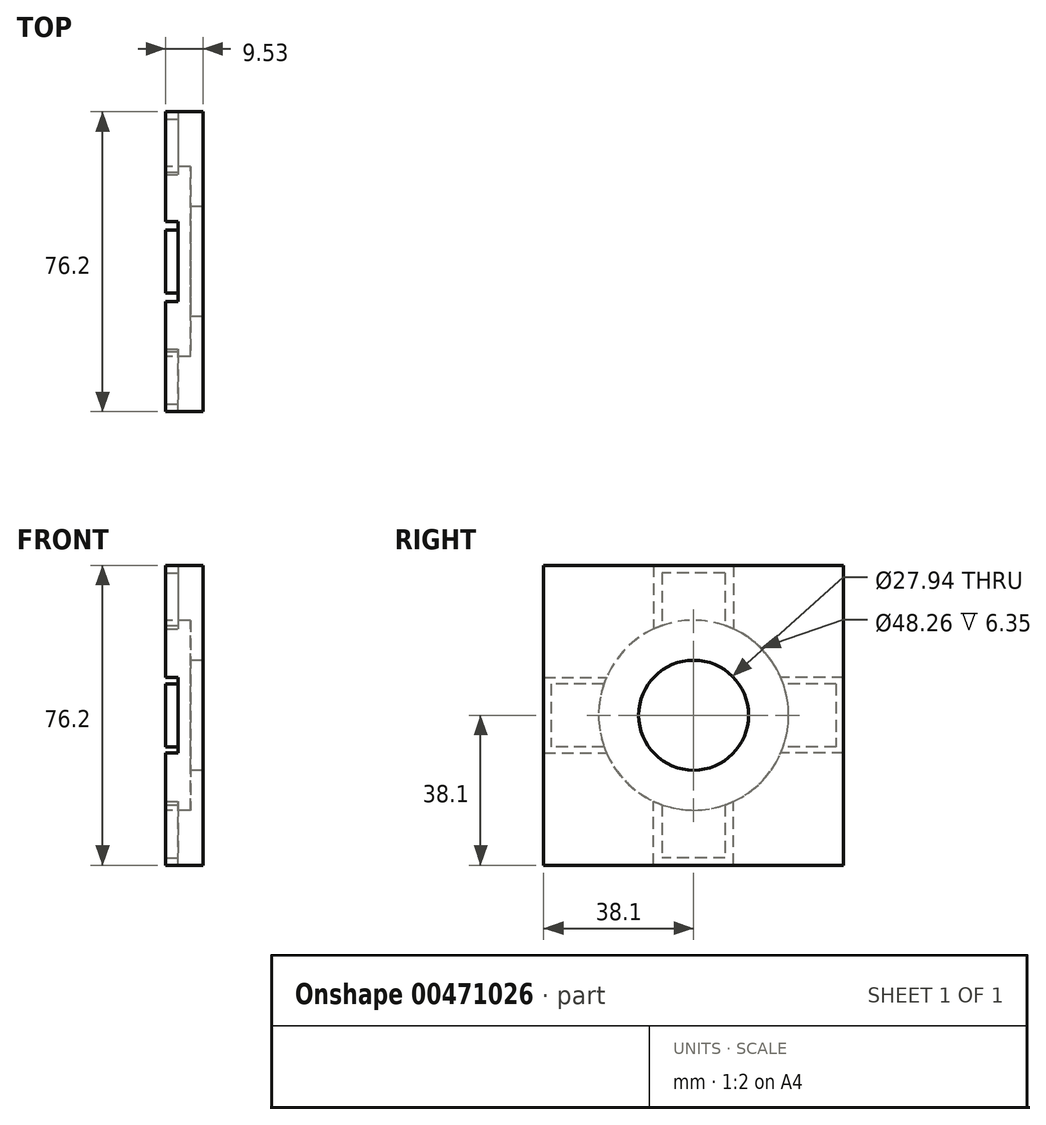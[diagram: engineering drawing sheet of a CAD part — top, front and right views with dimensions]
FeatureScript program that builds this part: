
annotation { "Feature Type Name" : "Feature", "Feature Type Description" : "" }
export const myFeature = defineFeature(function(context is Context, id is Id, definition is map)
    precondition{}
    {
        {
            var Q0;
            Q0=qCreatedBy(makeId("Right.planeOp"),FACE);
            var sketch = newSketch(context, id + "F0", { "sketchPlane" : qUnion([Q0])});
            skLineSegment(sketch, "E0.bottom", {"start": v(38.1, 38.1) * mm, "end": v(-38.1, 38.1) * mm});
            skLineSegment(sketch, "E0.top", {"start": v(38.1, -38.1) * mm, "end": v(-38.1, -38.1) * mm});
            skLineSegment(sketch, "E0.left", {"start": v(-38.1, -38.1) * mm, "end": v(-38.1, 38.1) * mm});
            skLineSegment(sketch, "E0.right", {"start": v(38.1, -38.1) * mm, "end": v(38.1, 38.1) * mm});
            skPoint(sketch, "E0.middle", {"position": v(0, 0) * mm});
            skCircle(sketch, "E1", {"center": v(0, 0) * mm, "radius": 24.13 * mm});
            skCircle(sketch, "E2.0", {"center": v(0, 0) * mm, "radius": 13.97 * mm});
            skSolve(sketch);
        }
        {
            var Q0;
            Q0=makeQuery(id+"F0.imprint","IMPRINT",FACE,{"disambiguationData":[TD([[makeQuery(id+"F0.imprint","IMPRINT",EDGE,{"derivedFrom":sQuery(id+"F0.wireOp",EDGE,"E0.bottom")}),1.0]])]});
            var Q1;
            Q1=makeQuery(id+"F0.imprint","IMPRINT",FACE,{"disambiguationData":[TD([[makeQuery(id+"F0.imprint","IMPRINT",EDGE,{"derivedFrom":sQuery(id+"F0.wireOp",EDGE,"E1")}),1.0]])]});
            var Q2;
            Q2=makeQuery(id+"F0.imprint","IMPRINT",FACE,{"disambiguationData":[TD([[makeQuery(id+"F0.imprint","IMPRINT",EDGE,{"derivedFrom":sQuery(id+"F0.wireOp",EDGE,"E2.0")}),-1.0]])]});
            extrude(context, id + "F1", {"entities" : qUnion([Q0, Q1, Q2]), "depth" : 6.35 * mm});
        }
        {
            var Q0;
            Q0=makeQuery(id+"F0.imprint","IMPRINT",FACE,{"disambiguationData":[TD([[makeQuery(id+"F0.imprint","IMPRINT",EDGE,{"derivedFrom":sQuery(id+"F0.wireOp",EDGE,"E1")}),1.0]])]});
            extrude(context, id + "F3", {"entities" : qUnion([Q0]), "operationType" : NewBodyOperationType.REMOVE, "depth" : 3.17 * mm});
        }
        {
            var Q0;
            Q0=makeQuery(id+"F0.imprint","IMPRINT",FACE,{"disambiguationData":[TD([[makeQuery(id+"F0.imprint","IMPRINT",EDGE,{"derivedFrom":sQuery(id+"F0.wireOp",EDGE,"E2.0")}),-1.0]])]});
            var sketch = newSketch(context, id + "F4", { "sketchPlane" : qUnion([Q0])});
            skLineSegment(sketch, "E3", {"start": v(0, 5.4) * mm, "end": v(0, -5.41) * mm});
            skFitSpline(sketch, "E4", {"points": [v(0, -5.41) * mm, v(-4.57, -2.66) * mm, v(-6.75, 1.98) * mm, v(-3.43, 6.35) * mm, v(0, 5.4) * mm], "startDerivative": vector(-18.4, 8.73) * mm, "endDerivative": vector(15.63, -9.22) * mm});
            skFitSpline(sketch, "E5", {"points": [v(-1.12, 6.06) * mm, v(0, 3.12) * mm], "startDerivative": vector(1.12, -2.93) * mm, "endDerivative": vector(1.12, -2.93) * mm});
            skFitSpline(sketch, "E6.MirrorCS", {"points": [v(0, -5.41) * mm, v(4.57, -2.66) * mm, v(6.75, 1.98) * mm, v(3.43, 6.35) * mm, v(0, 5.4) * mm], "startDerivative": vector(18.4, 8.73) * mm, "endDerivative": vector(-15.63, -9.22) * mm});
            skSolve(sketch);
        }
        {
            var Q0;
            Q0=makeQuery(id+"F0.imprint","IMPRINT",FACE,{"disambiguationData":[TD([[makeQuery(id+"F0.imprint","IMPRINT",EDGE,{"derivedFrom":sQuery(id+"F0.wireOp",EDGE,"E0.bottom")}),1.0]])]});
            var sketch = newSketch(context, id + "F5", { "sketchPlane" : qUnion([Q0])});
            skLineSegment(sketch, "E7.0", {"start": v(38.1, 38.1) * mm, "end": v(-38.1, 38.1) * mm});
            skLineSegment(sketch, "E7.1", {"start": v(38.1, -38.1) * mm, "end": v(38.1, 38.1) * mm});
            skLineSegment(sketch, "E7.2", {"start": v(38.1, -38.1) * mm, "end": v(10.16, -38.1) * mm});
            skLineSegment(sketch, "E7.3", {"start": v(-38.1, -38.1) * mm, "end": v(-38.1, -9.59) * mm});
            skArc(sketch, "E7.4", {"start": v(10.16, -21.89) * mm, "mid": v(17.28, -16.84) * mm, "end": v(22.14, -9.59) * mm});
            skLineSegment(sketch, "E8.bottom", {"start": v(38.1, 38.1) * mm, "end": v(10.16, 38.1) * mm});
            skLineSegment(sketch, "E8.top", {"start": v(38.1, 9.59) * mm, "end": v(22.14, 9.59) * mm});
            skLineSegment(sketch, "E8.left", {"start": v(38.1, 38.1) * mm, "end": v(38.1, 9.59) * mm});
            skLineSegment(sketch, "E8.right", {"start": v(10.16, 38.1) * mm, "end": v(10.16, 21.89) * mm});
            skLineSegment(sketch, "E9.bottom", {"start": v(-38.1, 38.1) * mm, "end": v(-10.16, 38.1) * mm});
            skLineSegment(sketch, "E9.top", {"start": v(-38.1, 9.59) * mm, "end": v(-22.14, 9.59) * mm});
            skLineSegment(sketch, "E9.left", {"start": v(-38.1, 38.1) * mm, "end": v(-38.1, 9.59) * mm});
            skLineSegment(sketch, "E9.right", {"start": v(-10.16, 38.1) * mm, "end": v(-10.16, 21.89) * mm});
            skLineSegment(sketch, "E10.top", {"start": v(38.1, -9.59) * mm, "end": v(22.14, -9.59) * mm});
            skLineSegment(sketch, "E10.left", {"start": v(38.1, -38.1) * mm, "end": v(38.1, -9.59) * mm});
            skLineSegment(sketch, "E10.right", {"start": v(10.16, -38.1) * mm, "end": v(10.16, -21.89) * mm});
            skLineSegment(sketch, "E11.bottom", {"start": v(-38.1, -38.1) * mm, "end": v(-10.16, -38.1) * mm});
            skLineSegment(sketch, "E11.top", {"start": v(-38.1, -9.59) * mm, "end": v(-22.14, -9.59) * mm});
            skLineSegment(sketch, "E11.right", {"start": v(-10.16, -38.1) * mm, "end": v(-10.16, -21.89) * mm});
            skLineSegment(sketch, "E12.bottom", {"start": v(36.2, 8) * mm, "end": v(22.76, 8) * mm});
            skLineSegment(sketch, "E12.top", {"start": v(36.2, -8) * mm, "end": v(22.76, -8) * mm});
            skLineSegment(sketch, "E12.left", {"start": v(36.2, 8) * mm, "end": v(36.2, -8) * mm});
            skLineSegment(sketch, "E12.right", {"start": v(-36.2, 8) * mm, "end": v(-36.2, -8) * mm});
            skLineSegment(sketch, "E13.bottom", {"start": v(8, 36.2) * mm, "end": v(-8, 36.2) * mm});
            skLineSegment(sketch, "E13.top", {"start": v(8, -36.2) * mm, "end": v(-8, -36.2) * mm});
            skLineSegment(sketch, "E13.left", {"start": v(8, 36.2) * mm, "end": v(8, 22.76) * mm});
            skLineSegment(sketch, "E13.right", {"start": v(-8, 36.2) * mm, "end": v(-8, 22.76) * mm});
            skLineSegment(sketch, "E14.trimOffspring", {"start": v(-22.76, 8) * mm, "end": v(-36.2, 8) * mm});
            skLineSegment(sketch, "E15.trimOffspring", {"start": v(-22.76, -8) * mm, "end": v(-36.2, -8) * mm});
            skLineSegment(sketch, "E16.trimOffspring", {"start": v(-8, -22.76) * mm, "end": v(-8, -36.2) * mm});
            skLineSegment(sketch, "E17.trimOffspring", {"start": v(8, -22.76) * mm, "end": v(8, -36.2) * mm});
            skLineSegment(sketch, "E18.trimOffspring", {"start": v(-38.1, 9.59) * mm, "end": v(-38.1, 38.1) * mm});
            skLineSegment(sketch, "E19.trimOffspring", {"start": v(-10.16, -38.1) * mm, "end": v(-38.1, -38.1) * mm});
            skArc(sketch, "E20.trimOffspring", {"start": v(-8, -22.76) * mm, "mid": v(0, -24.13) * mm, "end": v(8, -22.76) * mm});
            skArc(sketch, "E21.trimOffspring", {"start": v(22.14, 9.59) * mm, "mid": v(17.28, 16.84) * mm, "end": v(10.16, 21.89) * mm});
            skArc(sketch, "E22.trimOffspring", {"start": v(22.76, -8) * mm, "mid": v(24.13, 0) * mm, "end": v(22.76, 8) * mm});
            skArc(sketch, "E23.trimOffspring", {"start": v(8, 22.76) * mm, "mid": v(0, 24.13) * mm, "end": v(-8, 22.76) * mm});
            skArc(sketch, "E24.trimOffspring", {"start": v(-10.16, 21.89) * mm, "mid": v(-17.28, 16.84) * mm, "end": v(-22.14, 9.59) * mm});
            skArc(sketch, "E25.trimOffspring", {"start": v(-22.76, 8) * mm, "mid": v(-24.13, 0) * mm, "end": v(-22.76, -8) * mm});
            skArc(sketch, "E26.trimOffspring", {"start": v(-22.14, -9.59) * mm, "mid": v(-17.28, -16.84) * mm, "end": v(-10.16, -21.89) * mm});
            skSolve(sketch);
        }
        {
            var Q0;
            Q0 = qSketchRegion(id + "F5", true);
            extrude(context, id + "F6", {"entities" : qUnion([Q0]), "operationType" : NewBodyOperationType.ADD, "oppositeDirection" : true, "depth" : 3.17 * mm});
        }
        {
            var Q0;
            {var subQ1=sQuery(id+"F4.wireOp",EDGE,"E3");var subQ3=sQuery(id+"F4.wireOp",EDGE,"E5");var subQ4=makeQuery(id+"F4.imprint","INTERSECT",VERTEX,{"derivedFrom":[subQ1,subQ3]});Q0=makeQuery(id+"F4.imprint","IMPRINT",FACE,{"disambiguationData":[TD([[makeQuery(id+"F4.imprint","IMPRINT",EDGE,{"disambiguationData":[TD([[subQ4,1.0]])],"derivedFrom":subQ3}),-1.0]])]});}
            var Q1;
            {var subQ0=sQuery(id+"F4.wireOp",EDGE,"E6.MirrorCS");Q1=makeQuery(id+"F4.imprint","IMPRINT",FACE,{"disambiguationData":[TD([[makeQuery(id+"F4.imprint","IMPRINT",EDGE,{"derivedFrom":subQ0}),1.0]])]});}
            extrude(context, id + "F7", {"entities" : qUnion([Q0, Q1]), "operationType" : NewBodyOperationType.REMOVE, "depth" : 3.17 * mm});
        }
    });
